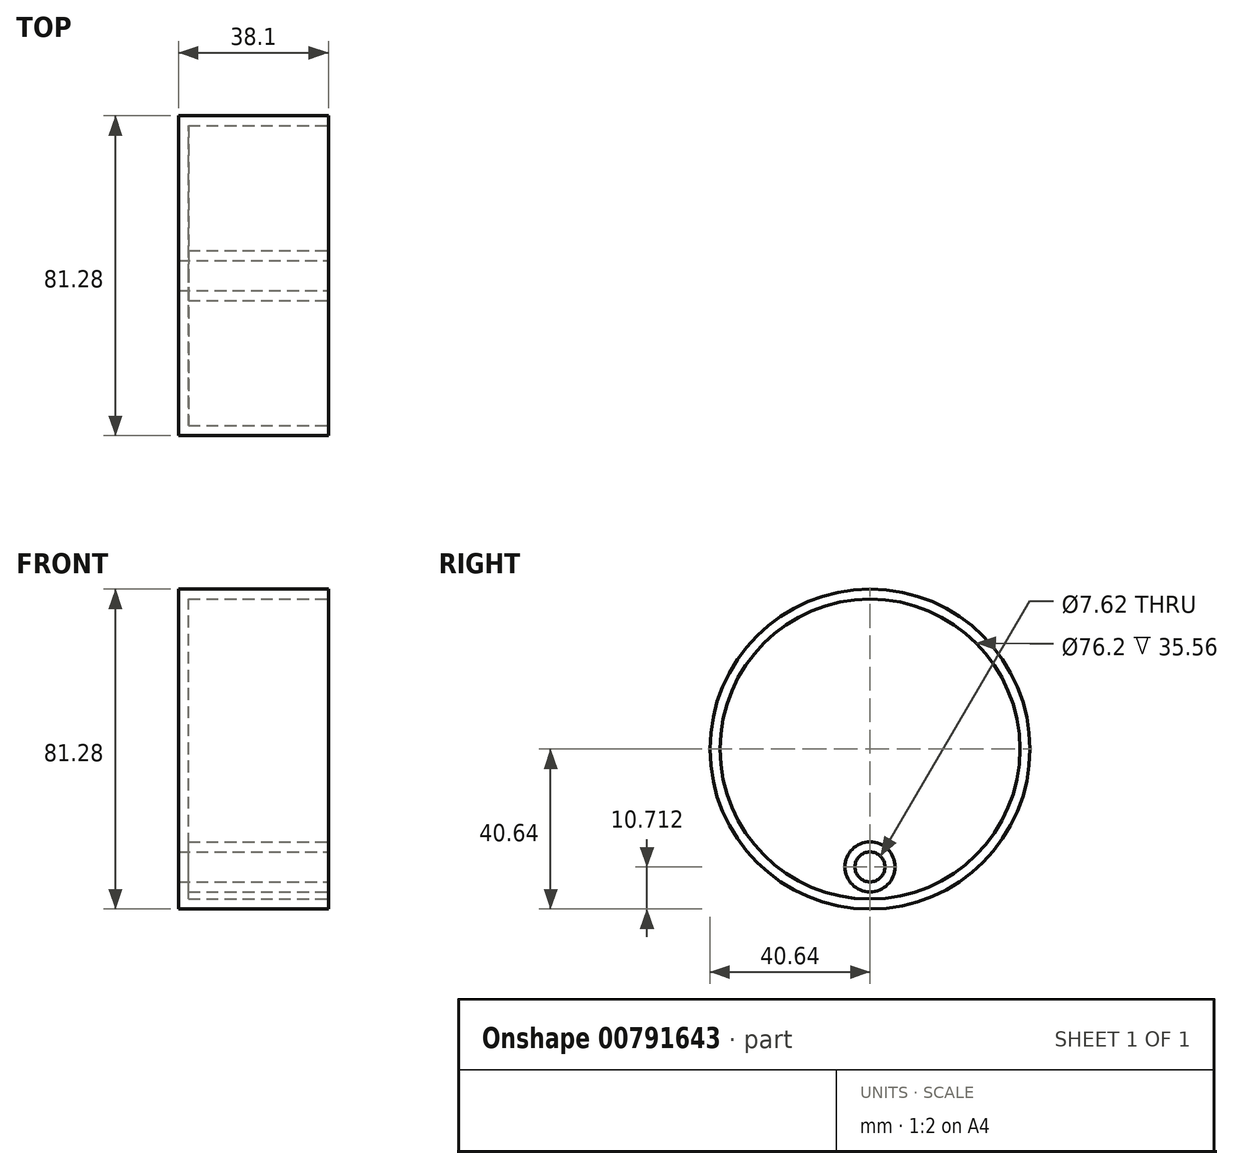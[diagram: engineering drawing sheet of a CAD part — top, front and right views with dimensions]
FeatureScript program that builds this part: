
annotation { "Feature Type Name" : "Feature", "Feature Type Description" : "" }
export const myFeature = defineFeature(function(context is Context, id is Id, definition is map)
    precondition{}
    {
        {
            var Q0;
            Q0=qCreatedBy(makeId("Right.planeOp"),FACE);
            var sketch = newSketch(context, id + "F0", { "sketchPlane" : qUnion([Q0])});
            skCircle(sketch, "E0", {"center": v(0, 0) * mm, "radius": 40.64 * mm});
            skCircle(sketch, "E1", {"center": v(0, -29.93) * mm, "radius": 3.81 * mm});
            skSolve(sketch);
        }
        {
            var Q0;
            Q0=qSketchRegion(id+"F0",true);
            extrude(context, id + "F1", {"entities" : qUnion([Q0]), "oppositeDirection" : true, "depth" : 38.1 * mm, "offsetDistance" : 25.4 * mm});
        }
        {
            var Q0;
            Q0=makeQuery(id+"F1.opExtrude","CAP_FACE",FACE,{"disambiguationData":[OSD([sQuery(id+"F0.wireOp",EDGE,"E0")])],"isStart":true});
            shell(context, id + "F2", {"entities" : qUnion([Q0]), "thickness" : 2.54 * mm});
        }
    });
